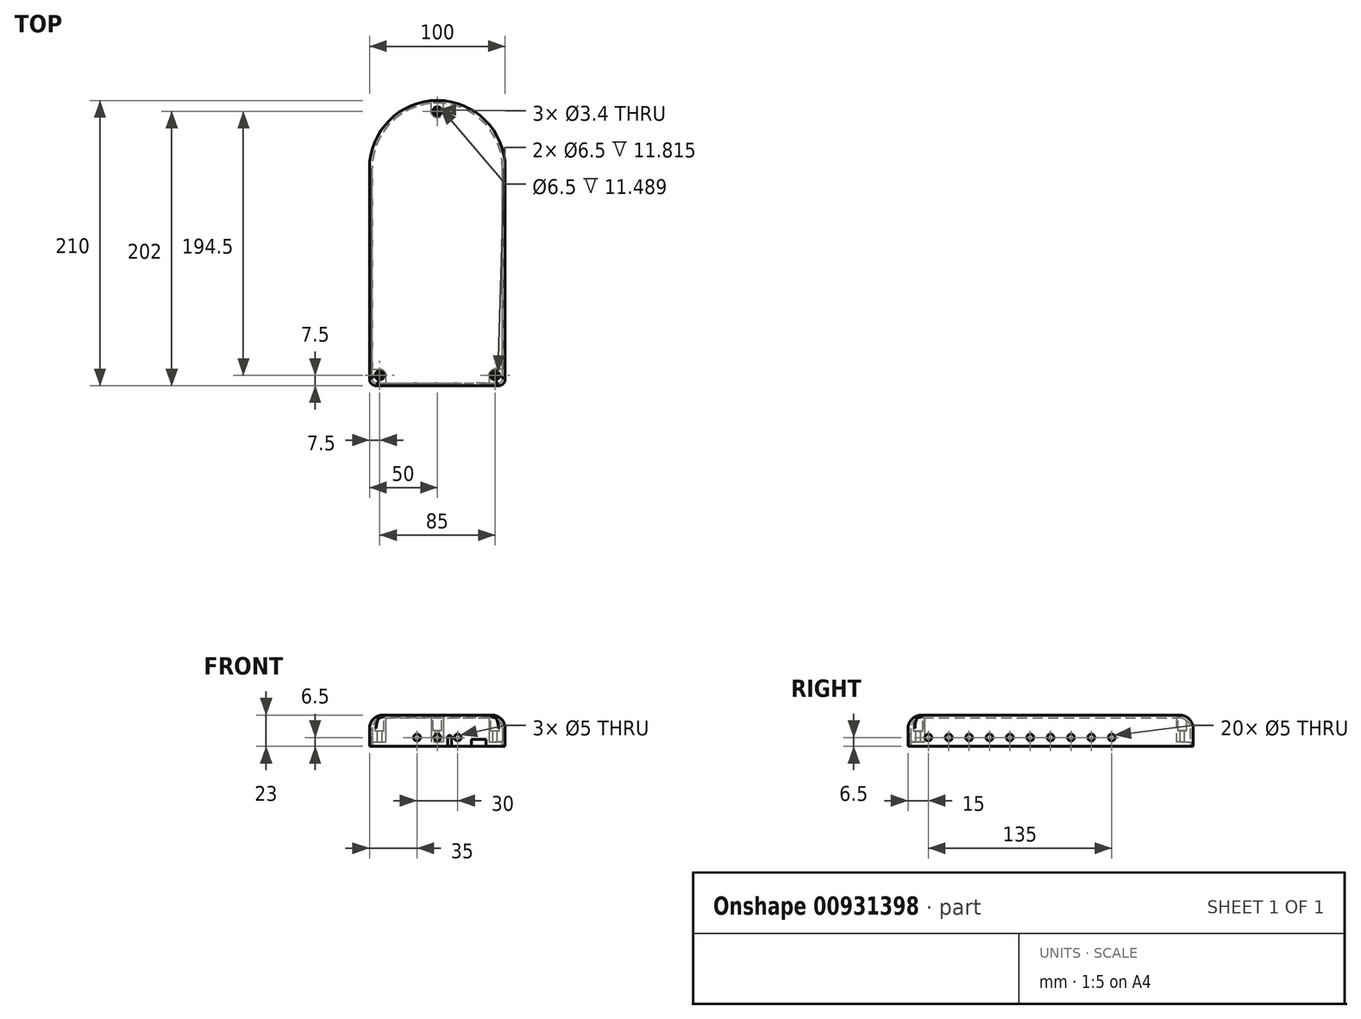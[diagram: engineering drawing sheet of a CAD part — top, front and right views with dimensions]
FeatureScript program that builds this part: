
annotation { "Feature Type Name" : "Feature", "Feature Type Description" : "" }
export const myFeature = defineFeature(function(context is Context, id is Id, definition is map)
    precondition{}
    {
        {
            var Q0;
            Q0=qCreatedBy(makeId("Top.planeOp"),FACE);
            var sketch = newSketch(context, id + "F0", { "sketchPlane" : qUnion([Q0])});
            skLineSegment(sketch, "E0.bottom", {"start": v(-45, -105) * mm, "end": v(45, -105) * mm});
            skLineSegment(sketch, "E0.top", {"start": v(0, 105) * mm, "end": v(0, 105) * mm});
            skLineSegment(sketch, "E0.left", {"start": v(-50, -100) * mm, "end": v(-50, 55) * mm});
            skLineSegment(sketch, "E0.right", {"start": v(50, -100) * mm, "end": v(50, 55) * mm});
            skPoint(sketch, "E1.visualSharp", {"position": v(-50, 105) * mm});
            skArc(sketch, "E1.filletArc", {"start": v(0, 105) * mm, "mid": v(-35.36, 90.36) * mm, "end": v(-50, 55) * mm});
            skPoint(sketch, "E2.visualSharp", {"position": v(50, 105) * mm});
            skArc(sketch, "E2.filletArc", {"start": v(50, 55) * mm, "mid": v(35.36, 90.36) * mm, "end": v(0, 105) * mm});
            skPoint(sketch, "E3.visualSharp", {"position": v(-50, -105) * mm});
            skArc(sketch, "E3.filletArc", {"start": v(-50, -100) * mm, "mid": v(-48.54, -103.54) * mm, "end": v(-45, -105) * mm});
            skPoint(sketch, "E4.visualSharp", {"position": v(50, -105) * mm});
            skArc(sketch, "E4.filletArc", {"start": v(45, -105) * mm, "mid": v(48.54, -103.54) * mm, "end": v(50, -100) * mm});
            skSolve(sketch);
        }
        {
            var Q0;
            Q0=makeQuery(id+"F0.imprint","IMPRINT",FACE,{"disambiguationData":[TD([[makeQuery(id+"F0.imprint","IMPRINT",EDGE,{"derivedFrom":sQuery(id+"F0.wireOp",EDGE,"E0.bottom")}),1.0]])]});
            extrude(context, id + "F1", {"entities" : qUnion([Q0]), "depth" : 23 * mm, "offsetDistance" : 25 * mm});
        }
        {
            var Q0;
            Q0=makeQuery(id+"F1.opExtrude","CAP_EDGE",EDGE,{"disambiguationData":[OSD([sQuery(id+"F0.wireOp",EDGE,"E0.left")])],"isStart":false});
            fillet(context, id + "F2", {"entities" : qUnion([Q0]), "radius" : 10 * mm, "tangentPropagation" : true, "allowEdgeOverflow" : false});
        }
        {
            var Q0;
            Q0=makeQuery(id+"F1.opExtrude","CAP_FACE",FACE,{"disambiguationData":[OSD([sQuery(id+"F0.wireOp",EDGE,"E0.bottom"),sQuery(id+"F0.wireOp",EDGE,"E0.left"),sQuery(id+"F0.wireOp",EDGE,"E0.right"),sQuery(id+"F0.wireOp",EDGE,"E1.filletArc"),sQuery(id+"F0.wireOp",EDGE,"E2.filletArc"),sQuery(id+"F0.wireOp",EDGE,"E3.filletArc"),sQuery(id+"F0.wireOp",EDGE,"E4.filletArc")])],"isStart":true});
            shell(context, id + "F3", {"entities" : qUnion([Q0]), "thickness" : 2 * mm});
        }
        {
            var Q0;
            Q0=makeQuery(id+"F1.opExtrude","CAP_FACE",FACE,{"disambiguationData":[OSD([sQuery(id+"F0.wireOp",EDGE,"E0.bottom"),sQuery(id+"F0.wireOp",EDGE,"E0.left"),sQuery(id+"F0.wireOp",EDGE,"E0.right"),sQuery(id+"F0.wireOp",EDGE,"E1.filletArc"),sQuery(id+"F0.wireOp",EDGE,"E2.filletArc"),sQuery(id+"F0.wireOp",EDGE,"E3.filletArc"),sQuery(id+"F0.wireOp",EDGE,"E4.filletArc")])],"isStart":true});
            var sketch = newSketch(context, id + "F4", { "sketchPlane" : qUnion([Q0])});
            skArc(sketch, "E5", {"start": v(-42.5, 93) * mm, "mid": v(-39.32, 94.32) * mm, "end": v(-38, 97.5) * mm});
            skArc(sketch, "E6", {"start": v(38, 97.5) * mm, "mid": v(39.32, 94.32) * mm, "end": v(42.5, 93) * mm});
            skArc(sketch, "E7", {"start": v(4.5, -97) * mm, "mid": v(0, -92.5) * mm, "end": v(-4.5, -97) * mm});
            skLineSegment(sketch, "E8", {"start": v(38, 97.5) * mm, "end": v(38, 103) * mm});
            skLineSegment(sketch, "E9", {"start": v(38, 103) * mm, "end": v(48, 103) * mm});
            skLineSegment(sketch, "E10", {"start": v(48, 103) * mm, "end": v(48, 93) * mm});
            skLineSegment(sketch, "E11", {"start": v(48, 93) * mm, "end": v(42.5, 93) * mm});
            skLineSegment(sketch, "E12", {"start": v(-38, 97.5) * mm, "end": v(-38, 103) * mm});
            skLineSegment(sketch, "E13", {"start": v(-38, 103) * mm, "end": v(-48, 103) * mm});
            skLineSegment(sketch, "E14", {"start": v(-48, 103) * mm, "end": v(-48, 93) * mm});
            skLineSegment(sketch, "E15", {"start": v(-48, 93) * mm, "end": v(-42.5, 93) * mm});
            skLineSegment(sketch, "E16.top", {"start": v(-4.5, -104) * mm, "end": v(4.5, -104) * mm});
            skLineSegment(sketch, "E16.left", {"start": v(-4.5, -97) * mm, "end": v(-4.5, -104) * mm});
            skLineSegment(sketch, "E16.right", {"start": v(4.5, -97) * mm, "end": v(4.5, -104) * mm});
            skSolve(sketch);
        }
        {
            var Q0;
            Q0=makeQuery(id+"F4.imprint","IMPRINT",FACE,{"disambiguationData":[TD([[makeQuery(id+"F4.imprint","IMPRINT",EDGE,{"derivedFrom":sQuery(id+"F4.wireOp",EDGE,"E5")}),1.0]])]});
            var Q1;
            Q1=makeQuery(id+"F4.imprint","IMPRINT",FACE,{"disambiguationData":[TD([[makeQuery(id+"F4.imprint","IMPRINT",EDGE,{"derivedFrom":sQuery(id+"F4.wireOp",EDGE,"E6")}),1.0]])]});
            var Q2;
            {var subQ0=sQuery(id+"F4.wireOp",EDGE,"E7");Q2=makeQuery(id+"F4.imprint","IMPRINT",FACE,{"disambiguationData":[TD([[makeQuery(id+"F4.imprint","IMPRINT",EDGE,{"derivedFrom":subQ0}),1.0]])]});}
            extrude(context, id + "F5", {"entities" : qUnion([Q0, Q1, Q2]), "operationType" : NewBodyOperationType.ADD, "endBound" : BoundingType.UP_TO_NEXT, "oppositeDirection" : true, "depth" : 25 * mm, "offsetDistance" : 5 * mm, "offsetOppositeDirection" : true, "hasSecondDirection" : true, "secondDirectionOppositeDirection" : false, "secondDirectionDepth" : -3.2 * mm});
        }
        {
            var Q0;
            Q0=makeQuery(id+"F1.opExtrude","CAP_FACE",FACE,{"disambiguationData":[OSD([sQuery(id+"F0.wireOp",EDGE,"E0.bottom"),sQuery(id+"F0.wireOp",EDGE,"E0.left"),sQuery(id+"F0.wireOp",EDGE,"E0.right"),sQuery(id+"F0.wireOp",EDGE,"E1.filletArc"),sQuery(id+"F0.wireOp",EDGE,"E2.filletArc"),sQuery(id+"F0.wireOp",EDGE,"E3.filletArc"),sQuery(id+"F0.wireOp",EDGE,"E4.filletArc")])],"isStart":false});
            var sketch = newSketch(context, id + "F6", { "sketchPlane" : qUnion([Q0])});
            skPoint(sketch, "E17", {"position": v(0, 97) * mm});
            skPoint(sketch, "E18", {"position": v(-42.5, -97.5) * mm});
            skPoint(sketch, "E19", {"position": v(42.5, -97.5) * mm});
            skSolve(sketch);
        }
        {
            var Q0;
            Q0=sQuery(id+"F6.wireOp",VERTEX,"E17");
            var Q1;
            Q1=sQuery(id+"F6.wireOp",VERTEX,"E19");
            var Q2;
            Q2=sQuery(id+"F6.wireOp",VERTEX,"E18");
            var Q3;
            Q3=makeQuery(id+"F1.opExtrude","SWEPT_BODY",BODY,{"disambiguationData":[OSD([sQuery(id+"F0.wireOp",EDGE,"E0.bottom"),sQuery(id+"F0.wireOp",EDGE,"E0.left"),sQuery(id+"F0.wireOp",EDGE,"E0.right"),sQuery(id+"F0.wireOp",EDGE,"E1.filletArc"),sQuery(id+"F0.wireOp",EDGE,"E2.filletArc"),sQuery(id+"F0.wireOp",EDGE,"E3.filletArc"),sQuery(id+"F0.wireOp",EDGE,"E4.filletArc")])]});
            hole(context, id + "F7", {"style" : HoleStyle.C_BORE, "endStyle" : HoleEndStyle.THROUGH, "holeDiameter" : 3.4 * mm, "cBoreDiameter" : 6.5 * mm, "cBoreDepth" : 10 * mm, "majorDiameter" : 5 * mm, "isTappedThrough" : true, "tappedDepth" : 12 * mm, "tapClearance" : 3, "locations" : qUnion([Q0, Q1, Q2]), "scope" : qUnion([Q3])});
        }
        {
            var Q0;
            Q0=makeQuery(id+"F1.opExtrude","SWEPT_FACE",FACE,{"disambiguationData":[OSD([sQuery(id+"F0.wireOp",EDGE,"E0.bottom")])]});
            var sketch = newSketch(context, id + "F8", { "sketchPlane" : qUnion([Q0])});
            skArc(sketch, "E20", {"start": v(10.5, 6.5) * mm, "mid": v(9, 8) * mm, "end": v(7.5, 6.5) * mm});
            skLineSegment(sketch, "E21.top", {"start": v(7.5, 0) * mm, "end": v(10.5, 0) * mm});
            skLineSegment(sketch, "E21.left", {"start": v(7.5, 6.5) * mm, "end": v(7.5, 0) * mm});
            skLineSegment(sketch, "E21.right", {"start": v(10.5, 6.5) * mm, "end": v(10.5, 0) * mm});
            skCircle(sketch, "E22", {"center": v(0, 6.5) * mm, "radius": 2.5 * mm});
            skCircle(sketch, "E23.1.0.0", {"center": v(15, 6.5) * mm, "radius": 2.5 * mm});
            skLineSegment(sketch, "E23.direction1", {"start": v(0, 6.5) * mm, "end": v(15, 6.5) * mm, "construction": true});
            skCircle(sketch, "E24.1.0.0", {"center": v(-15, 6.5) * mm, "radius": 2.5 * mm});
            skCircle(sketch, "E24.2.0.0", {"center": v(-30, 6.5) * mm, "radius": 2.5 * mm});
            skLineSegment(sketch, "E24.direction1", {"start": v(0, 6.5) * mm, "end": v(-15, 6.5) * mm, "construction": true});
            skLineSegment(sketch, "E25.bottom", {"start": v(36, 0) * mm, "end": v(25, 0) * mm});
            skLineSegment(sketch, "E25.top", {"start": v(36, 5) * mm, "end": v(25, 5) * mm});
            skLineSegment(sketch, "E25.left", {"start": v(36, 0) * mm, "end": v(36, 5) * mm});
            skLineSegment(sketch, "E25.right", {"start": v(25, 0) * mm, "end": v(25, 5) * mm});
            skSolve(sketch);
        }
        {
            var Q0;
            Q0=makeQuery(id+"F8.imprint","IMPRINT",FACE,{"disambiguationData":[TD([[makeQuery(id+"F8.imprint","IMPRINT",EDGE,{"derivedFrom":sQuery(id+"F8.wireOp",EDGE,"E20")}),1.0]])]});
            var Q1;
            Q1=makeQuery(id+"F8.imprint","IMPRINT",FACE,{"disambiguationData":[TD([[makeQuery(id+"F8.imprint","IMPRINT",EDGE,{"derivedFrom":sQuery(id+"F8.wireOp",EDGE,"E23.1.0.0")}),1.0]])]});
            var Q2;
            Q2=makeQuery(id+"F8.imprint","IMPRINT",FACE,{"disambiguationData":[TD([[makeQuery(id+"F8.imprint","IMPRINT",EDGE,{"derivedFrom":sQuery(id+"F8.wireOp",EDGE,"E23.2.0.0")}),1.0]])]});
            var Q3;
            Q3=makeQuery(id+"F8.imprint","IMPRINT",FACE,{"disambiguationData":[TD([[makeQuery(id+"F8.imprint","IMPRINT",EDGE,{"derivedFrom":sQuery(id+"F8.wireOp",EDGE,"E22")}),1.0]])]});
            var Q4;
            Q4=makeQuery(id+"F8.imprint","IMPRINT",FACE,{"disambiguationData":[TD([[makeQuery(id+"F8.imprint","IMPRINT",EDGE,{"derivedFrom":sQuery(id+"F8.wireOp",EDGE,"E24.1.0.0")}),1.0]])]});
            var Q5;
            Q5=makeQuery(id+"F8.imprint","IMPRINT",FACE,{"disambiguationData":[TD([[makeQuery(id+"F8.imprint","IMPRINT",EDGE,{"derivedFrom":sQuery(id+"F8.wireOp",EDGE,"E25.bottom")}),1.0]])]});
            extrude(context, id + "F9", {"entities" : qUnion([Q0, Q1, Q2, Q3, Q4, Q5]), "operationType" : NewBodyOperationType.REMOVE, "endBound" : BoundingType.UP_TO_NEXT, "oppositeDirection" : true, "depth" : 25 * mm, "offsetDistance" : 25 * mm});
        }
        {
            var Q0;
            Q0=makeQuery(id+"F1.opExtrude","SWEPT_FACE",FACE,{"disambiguationData":[OSD([sQuery(id+"F0.wireOp",EDGE,"E0.left")])]});
            var sketch = newSketch(context, id + "F10", { "sketchPlane" : qUnion([Q0])});
            skCircle(sketch, "E26", {"center": v(-45, 6.5) * mm, "radius": 2.5 * mm});
            skCircle(sketch, "E27.1.0.0", {"center": v(-30, 6.5) * mm, "radius": 2.5 * mm});
            skCircle(sketch, "E27.2.0.0", {"center": v(-15, 6.5) * mm, "radius": 2.5 * mm});
            skCircle(sketch, "E27.3.0.0", {"center": v(0, 6.5) * mm, "radius": 2.5 * mm});
            skCircle(sketch, "E27.4.0.0", {"center": v(15, 6.5) * mm, "radius": 2.5 * mm});
            skCircle(sketch, "E27.5.0.0", {"center": v(30, 6.5) * mm, "radius": 2.5 * mm});
            skCircle(sketch, "E27.6.0.0", {"center": v(45, 6.5) * mm, "radius": 2.5 * mm});
            skCircle(sketch, "E27.7.0.0", {"center": v(60, 6.5) * mm, "radius": 2.5 * mm});
            skCircle(sketch, "E27.8.0.0", {"center": v(75, 6.5) * mm, "radius": 2.5 * mm});
            skCircle(sketch, "E27.9.0.0", {"center": v(90, 6.5) * mm, "radius": 2.5 * mm});
            skLineSegment(sketch, "E27.direction1", {"start": v(-45, 6.5) * mm, "end": v(-30, 6.5) * mm, "construction": true});
            skSolve(sketch);
        }
        {
            var Q0;
            Q0=makeQuery(id+"F10.imprint","IMPRINT",FACE,{"disambiguationData":[TD([[makeQuery(id+"F10.imprint","IMPRINT",EDGE,{"derivedFrom":sQuery(id+"F10.wireOp",EDGE,"E26")}),1.0]])]});
            var Q1;
            Q1=makeQuery(id+"F10.imprint","IMPRINT",FACE,{"disambiguationData":[TD([[makeQuery(id+"F10.imprint","IMPRINT",EDGE,{"derivedFrom":sQuery(id+"F10.wireOp",EDGE,"E27.1.0.0")}),1.0]])]});
            var Q2;
            Q2=makeQuery(id+"F10.imprint","IMPRINT",FACE,{"disambiguationData":[TD([[makeQuery(id+"F10.imprint","IMPRINT",EDGE,{"derivedFrom":sQuery(id+"F10.wireOp",EDGE,"E27.2.0.0")}),1.0]])]});
            var Q3;
            Q3=makeQuery(id+"F10.imprint","IMPRINT",FACE,{"disambiguationData":[TD([[makeQuery(id+"F10.imprint","IMPRINT",EDGE,{"derivedFrom":sQuery(id+"F10.wireOp",EDGE,"E27.3.0.0")}),1.0]])]});
            var Q4;
            Q4=makeQuery(id+"F10.imprint","IMPRINT",FACE,{"disambiguationData":[TD([[makeQuery(id+"F10.imprint","IMPRINT",EDGE,{"derivedFrom":sQuery(id+"F10.wireOp",EDGE,"E27.4.0.0")}),1.0]])]});
            var Q5;
            Q5=makeQuery(id+"F10.imprint","IMPRINT",FACE,{"disambiguationData":[TD([[makeQuery(id+"F10.imprint","IMPRINT",EDGE,{"derivedFrom":sQuery(id+"F10.wireOp",EDGE,"E27.5.0.0")}),1.0]])]});
            var Q6;
            Q6=makeQuery(id+"F10.imprint","IMPRINT",FACE,{"disambiguationData":[TD([[makeQuery(id+"F10.imprint","IMPRINT",EDGE,{"derivedFrom":sQuery(id+"F10.wireOp",EDGE,"E27.6.0.0")}),1.0]])]});
            var Q7;
            Q7=makeQuery(id+"F10.imprint","IMPRINT",FACE,{"disambiguationData":[TD([[makeQuery(id+"F10.imprint","IMPRINT",EDGE,{"derivedFrom":sQuery(id+"F10.wireOp",EDGE,"E27.7.0.0")}),1.0]])]});
            var Q8;
            Q8=makeQuery(id+"F10.imprint","IMPRINT",FACE,{"disambiguationData":[TD([[makeQuery(id+"F10.imprint","IMPRINT",EDGE,{"derivedFrom":sQuery(id+"F10.wireOp",EDGE,"E27.8.0.0")}),1.0]])]});
            var Q9;
            Q9=makeQuery(id+"F10.imprint","IMPRINT",FACE,{"disambiguationData":[TD([[makeQuery(id+"F10.imprint","IMPRINT",EDGE,{"derivedFrom":sQuery(id+"F10.wireOp",EDGE,"E27.9.0.0")}),1.0]])]});
            extrude(context, id + "F11", {"entities" : qUnion([Q0, Q1, Q2, Q3, Q4, Q5, Q6, Q7, Q8, Q9]), "operationType" : NewBodyOperationType.REMOVE, "endBound" : BoundingType.THROUGH_ALL, "oppositeDirection" : true, "depth" : 25 * mm, "offsetDistance" : 25 * mm});
        }
    });
